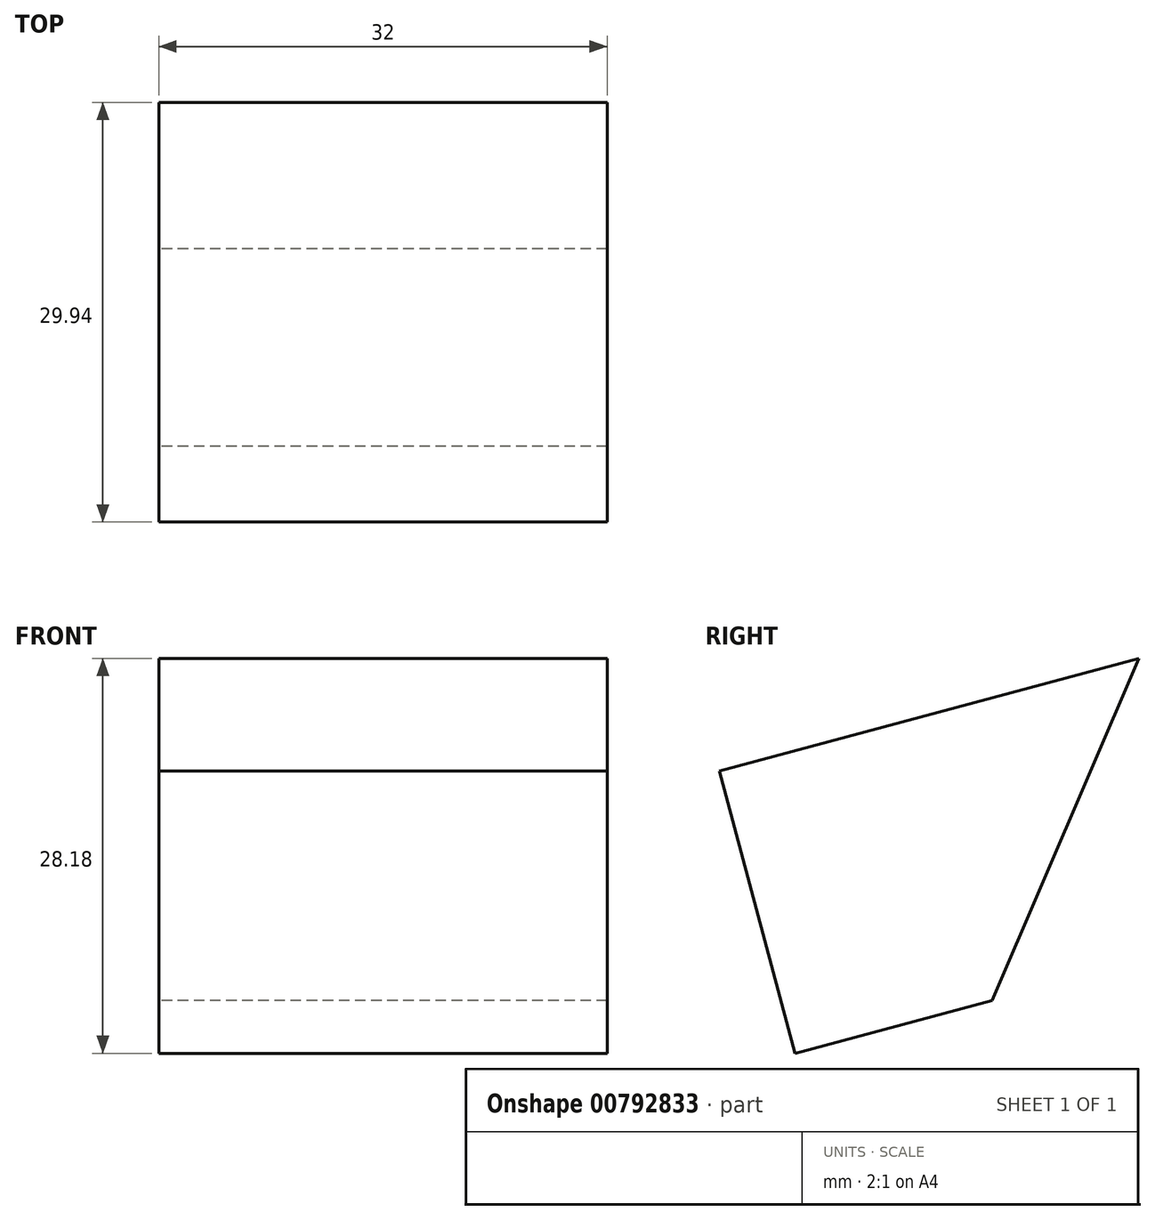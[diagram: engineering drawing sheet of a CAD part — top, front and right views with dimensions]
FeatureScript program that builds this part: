
annotation { "Feature Type Name" : "Feature", "Feature Type Description" : "" }
export const myFeature = defineFeature(function(context is Context, id is Id, definition is map)
    precondition{}
    {
        {
            var Q0;
            Q0=qCreatedBy(makeId("Right.planeOp"),FACE);
            var sketch = newSketch(context, id + "F0", { "sketchPlane" : qUnion([Q0])});
            skLineSegment(sketch, "E0", {"start": v(-67, 0) * mm, "end": v(78.93, 0) * mm, "construction": true});
            skLineSegment(sketch, "E1", {"start": v(0, 0) * mm, "end": v(29.94, 8.02) * mm});
            skLineSegment(sketch, "E2", {"start": v(0, 0) * mm, "end": v(5.4, -20.16) * mm});
            skLineSegment(sketch, "E3", {"start": v(29.94, 8.02) * mm, "end": v(19.48, -16.38) * mm});
            skLineSegment(sketch, "E4", {"start": v(5.4, -20.16) * mm, "end": v(19.48, -16.38) * mm});
            skSolve(sketch);
        }
        {
            var Q0;
            Q0 = qSketchRegion(id + "F0", true);
            extrude(context, id + "F1", {"entities" : qUnion([Q0]), "depth" : 32 * mm, "offsetDistance" : 25 * mm});
        }
    });
